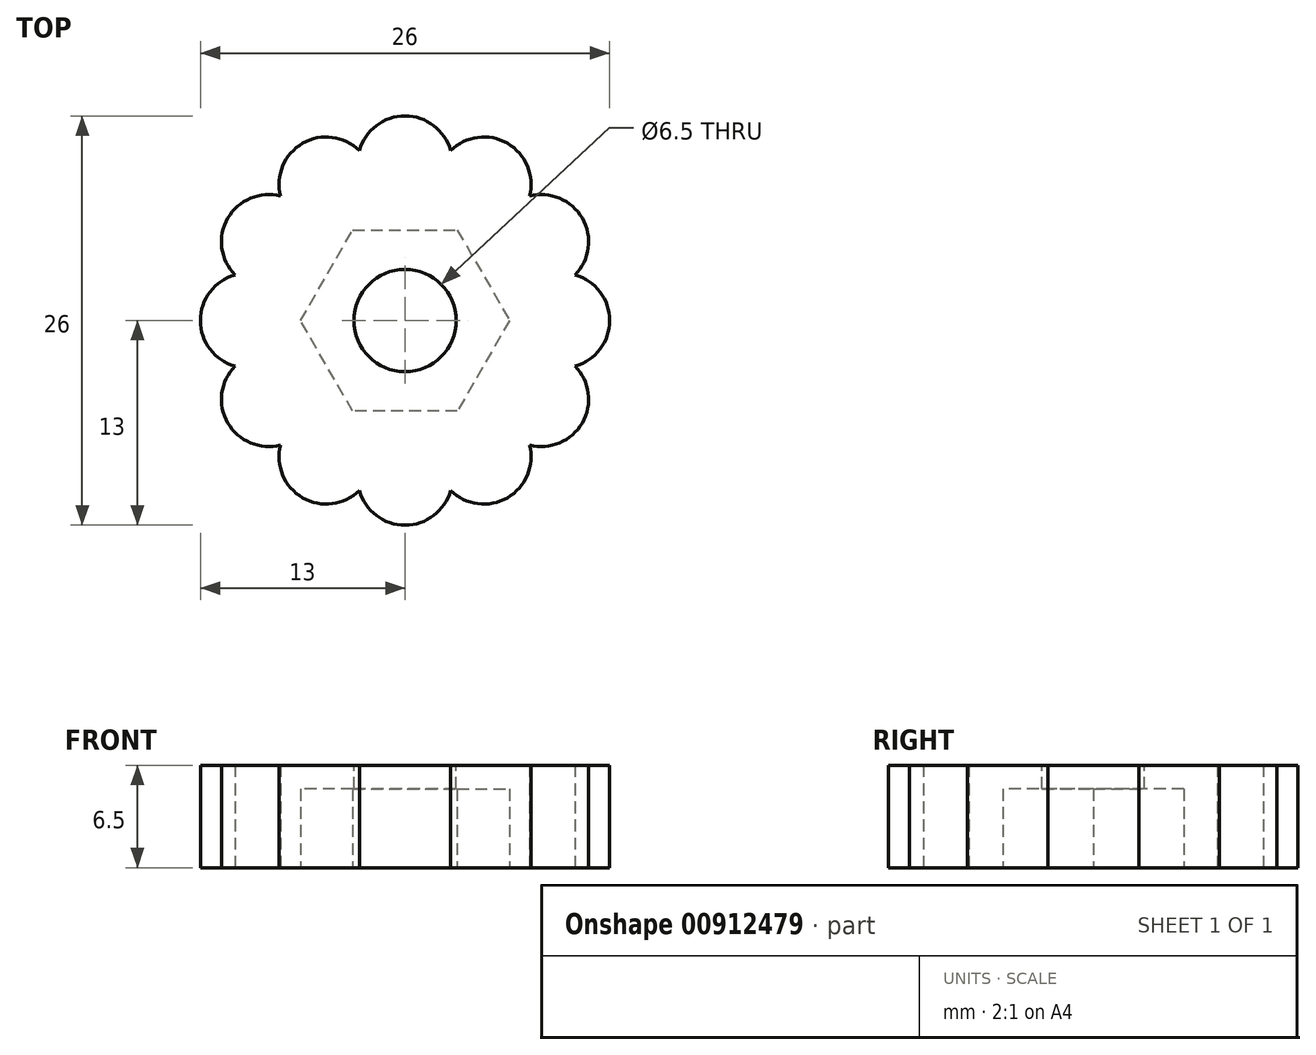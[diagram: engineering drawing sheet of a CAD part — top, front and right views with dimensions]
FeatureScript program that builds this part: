
annotation { "Feature Type Name" : "Feature", "Feature Type Description" : "" }
export const myFeature = defineFeature(function(context is Context, id is Id, definition is map)
    precondition{}
    {
        {
            var Q0;
            Q0=qCreatedBy(makeId("Top.planeOp"),FACE);
            var sketch = newSketch(context, id + "F0", { "sketchPlane" : qUnion([Q0])});
            skArc(sketch, "E0.1.0", {"start": v(-2.9, 10.8) * mm, "mid": v(-6.5, 11.26) * mm, "end": v(-7.9, 7.9) * mm});
            skPoint(sketch, "E0.center", {"position": v(0, 0) * mm});
            skArc(sketch, "E1.trimOffspring", {"start": v(2.9, 10.8) * mm, "mid": v(0, 13) * mm, "end": v(-2.9, 10.8) * mm});
            skArc(sketch, "E2.trimOffspring", {"start": v(7.9, 7.9) * mm, "mid": v(6.5, 11.26) * mm, "end": v(2.9, 10.8) * mm});
            skArc(sketch, "E3.trimOffspring", {"start": v(10.8, 2.9) * mm, "mid": v(11.26, 6.5) * mm, "end": v(7.9, 7.9) * mm});
            skArc(sketch, "E4.trimOffspring", {"start": v(10.8, -2.9) * mm, "mid": v(13, 0) * mm, "end": v(10.8, 2.9) * mm});
            skArc(sketch, "E5.trimOffspring", {"start": v(7.9, -7.9) * mm, "mid": v(11.26, -6.5) * mm, "end": v(10.8, -2.9) * mm});
            skArc(sketch, "E6.trimOffspring", {"start": v(2.9, -10.8) * mm, "mid": v(6.5, -11.26) * mm, "end": v(7.9, -7.9) * mm});
            skArc(sketch, "E7.trimOffspring", {"start": v(-2.9, -10.8) * mm, "mid": v(0, -13) * mm, "end": v(2.9, -10.8) * mm});
            skArc(sketch, "E8.trimOffspring", {"start": v(-7.9, -7.9) * mm, "mid": v(-6.5, -11.26) * mm, "end": v(-2.9, -10.8) * mm});
            skArc(sketch, "E9.trimOffspring", {"start": v(-10.8, -2.9) * mm, "mid": v(-11.26, -6.5) * mm, "end": v(-7.9, -7.9) * mm});
            skArc(sketch, "E10.trimOffspring", {"start": v(-10.8, 2.9) * mm, "mid": v(-13, 0) * mm, "end": v(-10.8, -2.9) * mm});
            skArc(sketch, "E11.trimOffspring", {"start": v(-7.9, 7.9) * mm, "mid": v(-11.26, 6.5) * mm, "end": v(-10.8, 2.9) * mm});
            skSolve(sketch);
        }
        {
            var Q0;
            Q0 = qSketchRegion(id + "F0", true);
            extrude(context, id + "F1", {"entities" : qUnion([Q0]), "depth" : 6.5 * mm, "offsetDistance" : 25 * mm});
        }
        {
            var Q0;
            Q0=makeQuery(id+"F1.opExtrude","CAP_FACE",FACE,{"disambiguationData":[OSD([sQuery(id+"F0.wireOp",EDGE,"gXGrQ610-2aJF-5Cjl-gTG7-OJwcLyXv3qiO"),sQuery(id+"F0.wireOp",EDGE,"QEJqaHNI-66CV-Fjeq-KHK1-WJLxKMQRhic0"),sQuery(id+"F0.wireOp",EDGE,"E0.1.0"),sQuery(id+"F0.wireOp",EDGE,"E0.2.0"),sQuery(id+"F0.wireOp",EDGE,"E0.3.0"),sQuery(id+"F0.wireOp",EDGE,"E0.4.0"),sQuery(id+"F0.wireOp",EDGE,"E0.5.0"),sQuery(id+"F0.wireOp",EDGE,"E0.6.0"),sQuery(id+"F0.wireOp",EDGE,"E0.7.0"),sQuery(id+"F0.wireOp",EDGE,"E0.8.0"),sQuery(id+"F0.wireOp",EDGE,"E0.9.0"),sQuery(id+"F0.wireOp",EDGE,"E0.10.0"),sQuery(id+"F0.wireOp",EDGE,"E0.11.0")])],"isStart":false});
            var sketch = newSketch(context, id + "F2", { "sketchPlane" : qUnion([Q0])});
            skCircle(sketch, "E12", {"center": v(0, 0) * mm, "radius": 3.25 * mm});
            skSolve(sketch);
        }
        {
            var Q0;
            Q0 = qSketchRegion(id + "F2", true);
            extrude(context, id + "F3", {"entities" : qUnion([Q0]), "operationType" : NewBodyOperationType.REMOVE, "oppositeDirection" : true, "depth" : 25 * mm, "offsetDistance" : 25 * mm});
        }
        {
            var Q0;
            Q0=qCreatedBy(makeId("Top.planeOp"),FACE);
            var sketch = newSketch(context, id + "F4", { "sketchPlane" : qUnion([Q0])});
            skCircle(sketch, "E13.cCircle", {"center": v(0, 0) * mm, "radius": 5.75 * mm, "construction": true});
            skLineSegment(sketch, "E13.0", {"start": v(-3.32, 5.75) * mm, "end": v(3.32, 5.75) * mm});
            skLineSegment(sketch, "E13.1", {"start": v(3.32, 5.75) * mm, "end": v(6.64, 0) * mm});
            skLineSegment(sketch, "E13.2", {"start": v(6.64, 0) * mm, "end": v(3.32, -5.75) * mm});
            skLineSegment(sketch, "E13.3", {"start": v(3.32, -5.75) * mm, "end": v(-3.32, -5.75) * mm});
            skLineSegment(sketch, "E13.4", {"start": v(-3.32, -5.75) * mm, "end": v(-6.64, 0) * mm});
            skLineSegment(sketch, "E13.5", {"start": v(-6.64, 0) * mm, "end": v(-3.32, 5.75) * mm});
            skPoint(sketch, "E13.0.midPoint", {"position": v(0, 5.75) * mm});
            skSolve(sketch);
        }
        {
            var Q0;
            Q0 = qSketchRegion(id + "F4", true);
            extrude(context, id + "F5", {"entities" : qUnion([Q0]), "operationType" : NewBodyOperationType.REMOVE, "depth" : 5 * mm, "offsetDistance" : 25 * mm});
        }
    });
